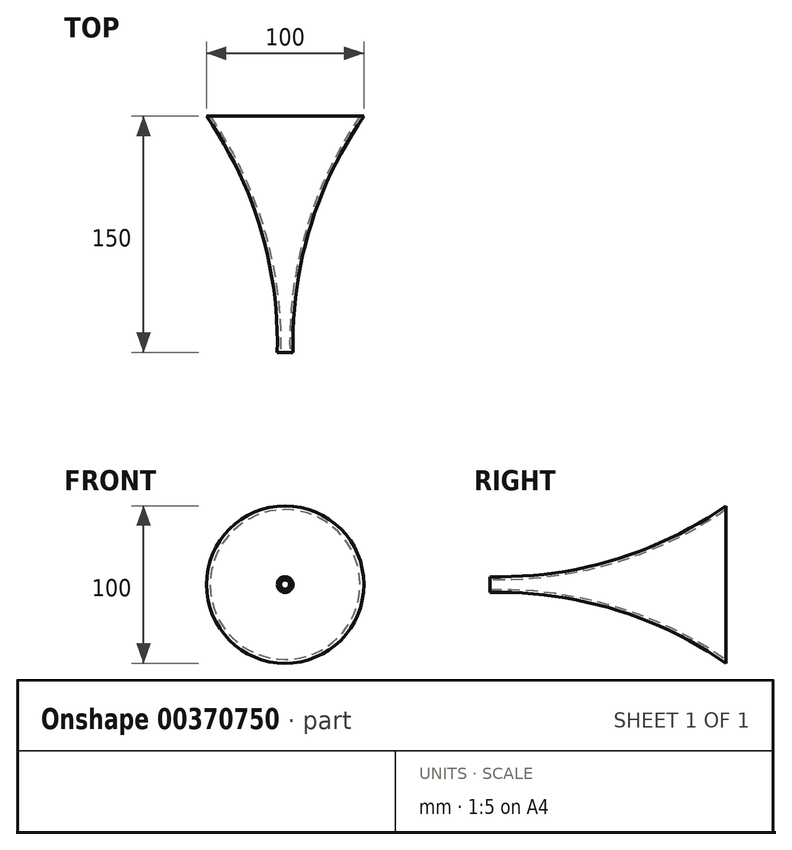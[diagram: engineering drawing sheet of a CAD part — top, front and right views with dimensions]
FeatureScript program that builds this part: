
annotation { "Feature Type Name" : "Feature", "Feature Type Description" : "" }
export const myFeature = defineFeature(function(context is Context, id is Id, definition is map)
    precondition{}
    {
        {
            var Q0;
            Q0=qCreatedBy(makeId("Right.planeOp"),FACE);
            var sketch = newSketch(context, id + "F0", { "sketchPlane" : qUnion([Q0])});
            skLineSegment(sketch, "E0", {"start": v(-102.82, 0) * mm, "end": v(86.32, 0) * mm, "construction": true});
            skLineSegment(sketch, "E1", {"start": v(-75, 3) * mm, "end": v(-75, 5) * mm});
            skLineSegment(sketch, "E2", {"start": v(75, 50) * mm, "end": v(75, 47.57) * mm});
            skArc(sketch, "E3", {"start": v(-75, 5) * mm, "mid": v(3.57, 15.6) * mm, "end": v(75, 50) * mm});
            skArc(sketch, "E4.0", {"start": v(-75, 3) * mm, "mid": v(3.5, 13.5) * mm, "end": v(75, 47.57) * mm});
            skPoint(sketch, "E5.orphan", {"position": v(75, 0) * mm});
            skPoint(sketch, "E6.orphan", {"position": v(-75, 0) * mm});
            skSolve(sketch);
        }
        {
            var Q0;
            Q0 = qSketchRegion(id + "F0", true);
            var Q1;
            Q1=sQuery(id+"F0.wireOp",EDGE,"E0");
            revolve(context, id + "F1", {"entities" : qUnion([Q0]), "axis" : qUnion([Q1]), "revolveType" : RevolveType.FULL});
        }
    });
